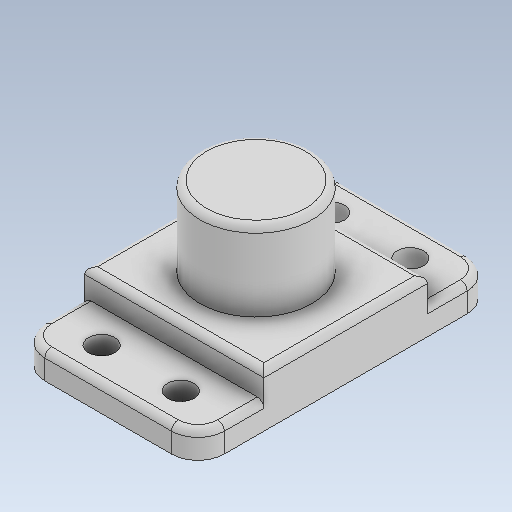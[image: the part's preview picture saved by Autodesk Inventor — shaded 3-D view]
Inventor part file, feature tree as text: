
AUTODESK INVENTOR PART (.ipt)
format: ipt  version: 2020.3 (Build 243373000, 373)  size: 183,808 bytes
history: native  units: mm
features: other x3, sketch x1
ambient origin geometry x8: Origin, YZ Plane, XZ Plane, XY Plane, X Axis, Y Axis, Z Axis, Center Point
bodies: Solid1 (feature_tree)
feature tree (4):
  other  "LegPin_v1.ipt"
  other  "Solid1::LegPin_v1.ipt"
  other  "TaggingFeature1"
  sketch  "Sketch1"  dims[d0=10.0mm]
